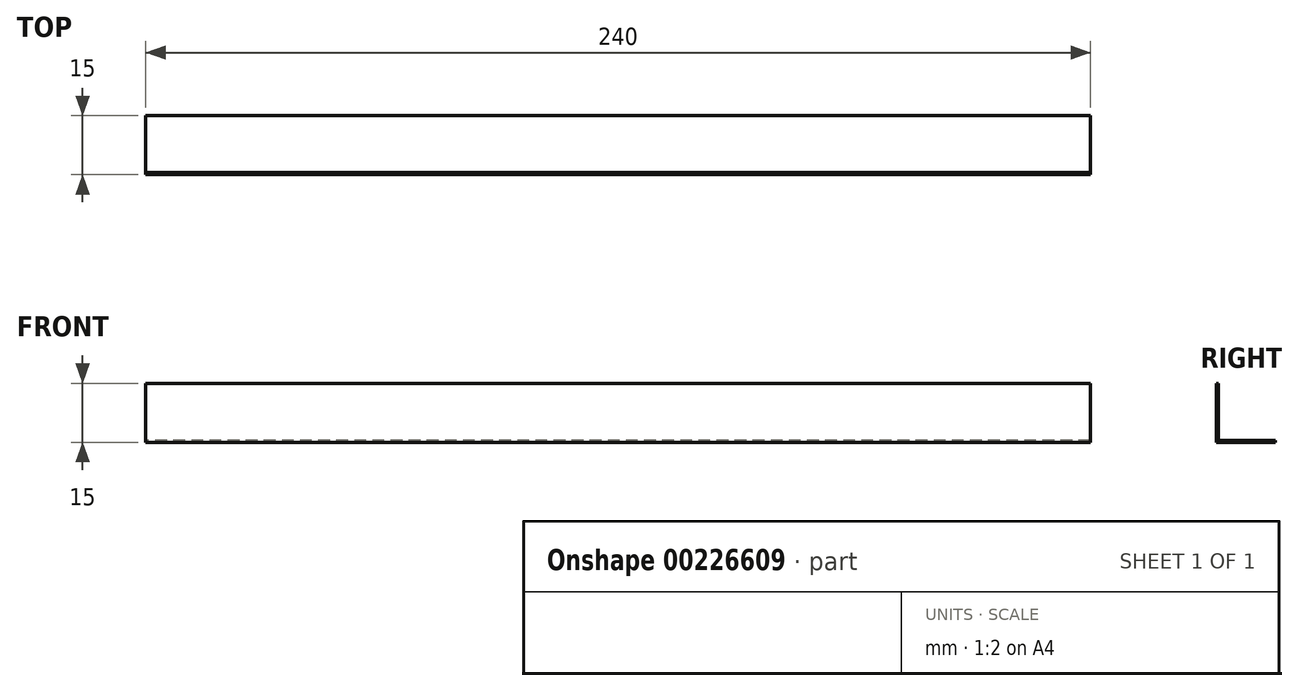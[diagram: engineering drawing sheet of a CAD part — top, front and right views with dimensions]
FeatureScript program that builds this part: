
annotation { "Feature Type Name" : "Feature", "Feature Type Description" : "" }
export const myFeature = defineFeature(function(context is Context, id is Id, definition is map)
    precondition{}
    {
        {
            var Q0;
            Q0=qCreatedBy(makeId("Right.planeOp"),FACE);
            var sketch = newSketch(context, id + "F0", { "sketchPlane" : qUnion([Q0])});
            skLineSegment(sketch, "E0", {"start": v(0, 0) * mm, "end": v(0, 15) * mm});
            skLineSegment(sketch, "E1", {"start": v(0, 15) * mm, "end": v(0.5, 15) * mm});
            skLineSegment(sketch, "E2", {"start": v(0.5, 15) * mm, "end": v(0.5, 0.5) * mm});
            skLineSegment(sketch, "E3", {"start": v(0.5, 0.5) * mm, "end": v(15, 0.5) * mm});
            skLineSegment(sketch, "E4", {"start": v(15, 0.5) * mm, "end": v(15, 0) * mm});
            skLineSegment(sketch, "E5", {"start": v(15, 0) * mm, "end": v(0, 0) * mm});
            skSolve(sketch);
        }
        {
            var Q0;
            Q0=makeQuery(id+"F0.imprint","IMPRINT",FACE,{"disambiguationData":[TD([[makeQuery(id+"F0.imprint","IMPRINT",EDGE,{"derivedFrom":sQuery(id+"F0.wireOp",EDGE,"E0")}),-1.0]])]});
            extrude(context, id + "F1", {"entities" : qUnion([Q0]), "endBound" : BoundingType.SYMMETRIC, "depth" : 240 * mm});
        }
    });
